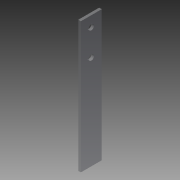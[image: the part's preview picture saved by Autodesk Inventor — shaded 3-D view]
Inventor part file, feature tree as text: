
AUTODESK INVENTOR PART (.ipt)
format: ipt  version: 2013 (Build 170138000, 138)  size: 76,288 bytes
history: native  units: in
note: dims shown in document units (in); Inventor stores cm internally (conversion verified against a paired STEP export)
features: extrude x1, sketch x1
ambient origin geometry x8: Origin, YZ Plane, XZ Plane, XY Plane, X Axis, Y Axis, Z Axis, Center Point
bodies: Solid1 (feature_tree)
feature tree (2):
  extrude  "Extrusion1"  Depth=1.0in
  sketch  "Sketch1"  dims[d0=6.25in d2=1.0in d3=0.26in d4=0.5in d5=1.25in d6=0.125in d7=0.0in]
